# Revit family: Medical-Other-Medical_Midmark_631-Procedure-Chair_1
name_source: partatom
category: Medical Equipment
units: mm (PartAtom-declared; Revit-internal decimal feet)

## family parameters
Always vertical = Yes
Cut with Voids When Loaded = No
Enable cutting in views = Yes
OmniClass Number = 23.40.70.11.14.21
OmniClass Title = Health Care Furniture
Part Type = Normal
Room Calculation Point = No
Round Connector Dimension = Use Diameter
Shared = No
Work Plane-Based = No

## types (1)
- 631-001 Procedure Chair
    Apparent Load = 1380 VA
    Classifications = Class I, Type B Applied Part Intermittent Operation [30 seconds ON / 5 minutes OFF]
    Connector Description = 115 VAC/60 Hz/12A
    Current = 12 A
    Default Elevation = 0 mm  [stored 0 ft]
    Description = Midmark 631 Procedure Chair (Non-Programmable) w/ Receptacle
    Height = 1929 mm  [stored 6.32874 ft]
    Length = 1900 mm  [stored 6.2336 ft]
    Manufacturer = Midmark
    Model = 631-001 Procedure Chair
    Number of Poles = 1
    Patient Weight (max) = 650.00 lbf
    Power Cord Length = 2438 mm
    Power Factor = 1
    Product Material = Upholstry-Midmark-Obsidian
    Product data url = https://bimobject.com
    Protection Against Ingress of Fluids = IPXO [Foot Control only: IPX1]
    Stirrup Weight Capacity = 73.71 kg (162.5 lb) each / 147.4 kg (325 lb) combined
    URL = http://www.midmark.com
    Version = 1
    Voltage = 115 V
    Weight = 565.00 lbf
    Width = 1260 mm  [stored 4.13386 ft]
    z_RP 0 = 0 mm  [stored 0 ft]

note: [stored X ft] marks values corroborated as IEEE doubles in the binary element streams (Revit-internal decimal feet)

## geometry (parser evidence)
native form markers: Sweep x9
no freeform markers — native parametric forms only
